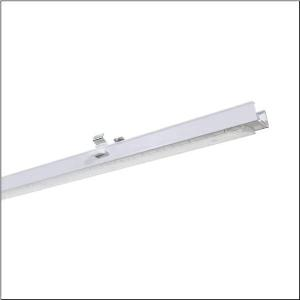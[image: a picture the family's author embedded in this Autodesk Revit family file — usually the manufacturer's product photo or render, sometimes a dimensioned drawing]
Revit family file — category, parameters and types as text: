
# Revit family: trunking_flex_31_51re12mb5cb
name_source: partatom
category: Lighting Fixtures
units: mm (PartAtom-declared; Revit-internal decimal feet)

## family parameters
Cut with Voids When Loaded = No
Host = Face
Light Source = No
Part Type = Normal
Room Calculation Point = No
Round Connector Dimension = Use Diameter
Shared = No

## types (1)
- --- (1 x LED, 11500 lm, 66 W, 5000K)
    Apparent Load = 66 VA
    CIE Flux Codes = 65 91 98 99 100
    Color Rendering = 80
    Color Temperature = 5000K
    Default Elevation = 1800 mm
    Description = Trunking Flex 31, luminaire insert, of extruded aluminium section, coated, traffic white (RAL 9016), length: 1.472mm, width: 91mm, height: 53mm, LED rated luminous flux: 11.500lm, light colour: 850, control gear: ON/OFF Multilumen, with system connector: socket, mains connection: 220..240V, AC, 50/60Hz, rated input power: 66W, luminous flux adjustable on luminaire in eight steps (3450/4380/5800/6700/8350/9200/10500/11500lm ), connected load according to luminous flux setting (19/24/32/37/47/52/60/66W), primary light control with lens, of plastic, primary optical cover: cover, of PMMA, light emission: direct distribution, protection rating (complete): IP20, insulation class (complete): insulation class I (protective earthing), certification: CE, UKCA, impact resistance: IK02, permissible ambient temperature for indoor applications: -20..+40°C, packaging unit: 1 piece
    Height = 58 mm
    Lamp = 1 x LED
    Lamp Light Flux = 11500 lm
    Lamp Power = 66 W
    Lamp count = 1
    Length = 1472 mm
    Luminous efficacy = 174 lm/W
    Manufacturer = Siteco
    ModVariant = No
    Model = 51RE12MB5CB
    Mounting Place = Ceiling
    Mounting Type = Pendant
    Number of Poles = 1
    OnlyDefault = Yes
    Power Factor = 1
    Product Name = Trunking Flex 31
    Product group = luminaire insert
    ProductGroupID = 901
    Protection Class = Protection class I
    Protection Degree = IP 20
    RLX_Detail_Level = 1
    RLX_Emergency_Light_Flux = 0 lm
    RLX_Emergency_Type = 0
    RLX_Emergency_Type_DB = No
    RlxData = <blob elided: 20989 chars, md5=43f4b17a>
    Socket = socket
    Standby Power = 0 W
    System Light Flux = 11500 lm
    System Power = 66 W
    Type Comments = factory setting: luminous flux: 100 % | (ON | ON | ON)
    Type Image = l_1266702.jpg
    URL = http://relux.com
    VarID = @adj_018617
    Voltage = 0 V
    Weight = 0.00 kg
    Width = 65 mm

## geometry (parser evidence)
native form markers: Blend x4, Sweep x10
no freeform markers — native parametric forms only
